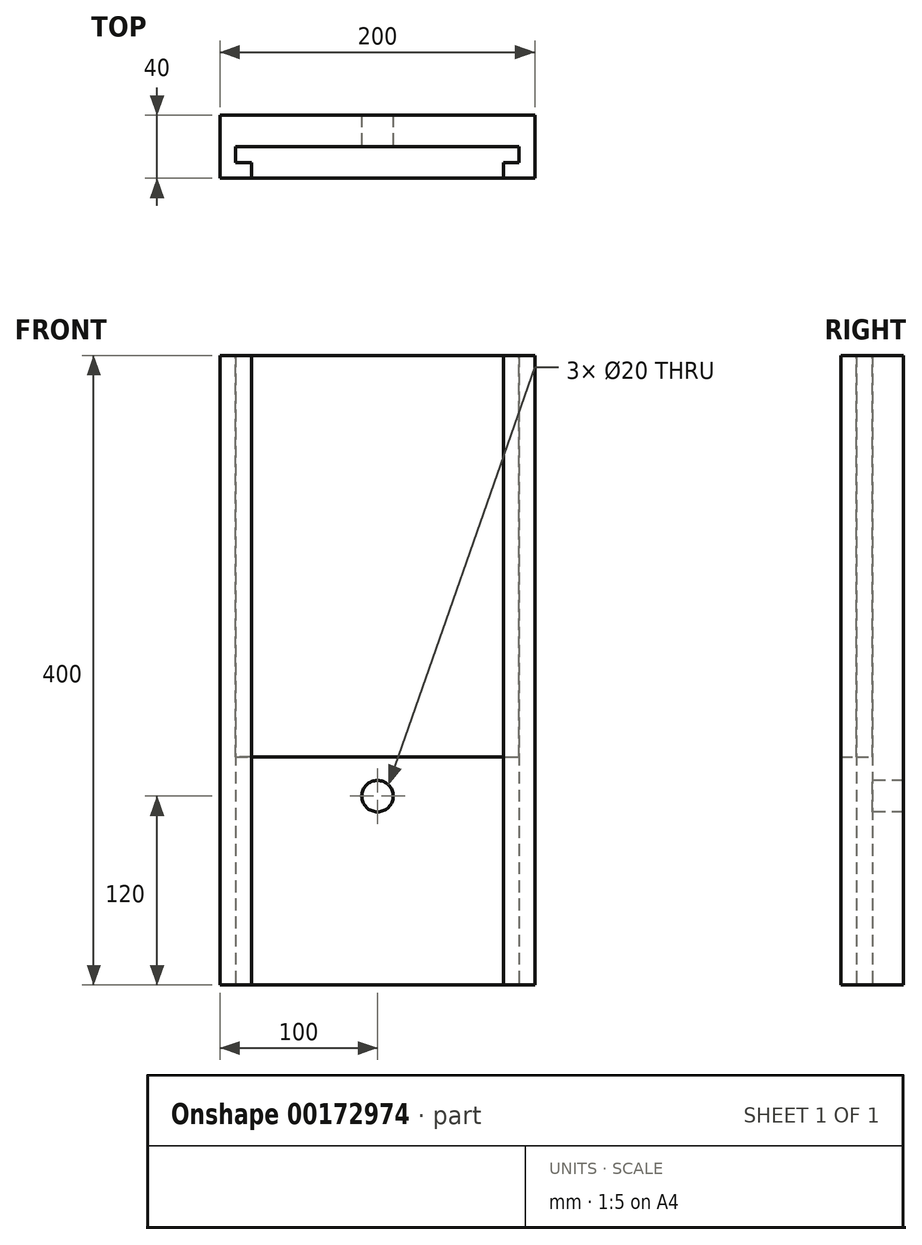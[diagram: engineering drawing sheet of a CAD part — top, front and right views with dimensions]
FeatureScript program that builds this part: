
annotation { "Feature Type Name" : "Feature", "Feature Type Description" : "" }
export const myFeature = defineFeature(function(context is Context, id is Id, definition is map)
    precondition{}
    {
        {
            var Q0;
            Q0=qCreatedBy(makeId("Top.planeOp"),FACE);
            var sketch = newSketch(context, id + "F0", { "sketchPlane" : qUnion([Q0])});
            skLineSegment(sketch, "E0", {"start": v(0, 40) * mm, "end": v(100, 40) * mm});
            skLineSegment(sketch, "E1", {"start": v(100, 40) * mm, "end": v(100, 0) * mm});
            skLineSegment(sketch, "E2", {"start": v(100, 0) * mm, "end": v(80, 0) * mm});
            skLineSegment(sketch, "E3", {"start": v(80, 0) * mm, "end": v(80, 10) * mm});
            skLineSegment(sketch, "E4", {"start": v(80, 10) * mm, "end": v(90, 10) * mm});
            skLineSegment(sketch, "E5", {"start": v(90, 10) * mm, "end": v(90, 20) * mm});
            skLineSegment(sketch, "E6", {"start": v(90, 20) * mm, "end": v(0, 20) * mm});
            skLineSegment(sketch, "E7", {"start": v(0, 40) * mm, "end": v(0, 0) * mm, "construction": true});
            skLineSegment(sketch, "E8.MirrorCS", {"start": v(0, 40) * mm, "end": v(-100, 40) * mm});
            skLineSegment(sketch, "E9.MirrorCS", {"start": v(-100, 40) * mm, "end": v(-100, 0) * mm});
            skLineSegment(sketch, "E10.MirrorCS", {"start": v(-100, 0) * mm, "end": v(-80, 0) * mm});
            skLineSegment(sketch, "E11.MirrorCS", {"start": v(-80, 0) * mm, "end": v(-80, 10) * mm});
            skLineSegment(sketch, "E12.MirrorCS", {"start": v(-80, 10) * mm, "end": v(-90, 10) * mm});
            skLineSegment(sketch, "E13.MirrorCS", {"start": v(-90, 10) * mm, "end": v(-90, 20) * mm});
            skLineSegment(sketch, "E14.MirrorCS", {"start": v(-90, 20) * mm, "end": v(0, 20) * mm});
            skSolve(sketch);
        }
        {
            var Q0;
            Q0=makeQuery(id+"F0.imprint","IMPRINT",FACE,{"disambiguationData":[TD([[makeQuery(id+"F0.imprint","IMPRINT",EDGE,{"derivedFrom":sQuery(id+"F0.wireOp",EDGE,"E0")}),-1.0]])]});
            extrude(context, id + "F1", {"entities" : qUnion([Q0]), "depth" : 280 * mm, "hasSecondDirection" : true, "secondDirectionOppositeDirection" : true, "secondDirectionDepth" : 120 * mm});
        }
        {
            var Q0;
            Q0=makeQuery(id+"F1.opExtrude","SWEPT_FACE",FACE,{"disambiguationData":[OSD([sQuery(id+"F0.wireOp",EDGE,"E6"),sQuery(id+"F0.wireOp",EDGE,"E14.MirrorCS")])]});
            var sketch = newSketch(context, id + "F2", { "sketchPlane" : qUnion([Q0])});
            skCircle(sketch, "E15", {"center": v(0, 0) * mm, "radius": 10 * mm});
            skSolve(sketch);
        }
        {
            var Q0;
            Q0 = qSketchRegion(id + "F2", true);
            extrude(context, id + "F3", {"entities" : qUnion([Q0]), "operationType" : NewBodyOperationType.REMOVE, "oppositeDirection" : true, "depth" : 20 * mm});
        }
        {
            var Q0;
            Q0=makeQuery(id+"F1.opExtrude","CAP_FACE",FACE,{"disambiguationData":[OSD([sQuery(id+"F0.wireOp",EDGE,"E0"),sQuery(id+"F0.wireOp",EDGE,"E1"),sQuery(id+"F0.wireOp",EDGE,"E2"),sQuery(id+"F0.wireOp",EDGE,"E3"),sQuery(id+"F0.wireOp",EDGE,"E4"),sQuery(id+"F0.wireOp",EDGE,"E5"),sQuery(id+"F0.wireOp",EDGE,"E6"),sQuery(id+"F0.wireOp",EDGE,"E8.MirrorCS"),sQuery(id+"F0.wireOp",EDGE,"E9.MirrorCS"),sQuery(id+"F0.wireOp",EDGE,"E10.MirrorCS"),sQuery(id+"F0.wireOp",EDGE,"E11.MirrorCS"),sQuery(id+"F0.wireOp",EDGE,"E12.MirrorCS"),sQuery(id+"F0.wireOp",EDGE,"E13.MirrorCS"),sQuery(id+"F0.wireOp",EDGE,"E14.MirrorCS")])],"isStart":false});
            var sketch = newSketch(context, id + "F4", { "sketchPlane" : qUnion([Q0])});
            skLineSegment(sketch, "E16", {"start": v(-90, 20) * mm, "end": v(-90, 10) * mm});
            skLineSegment(sketch, "E17", {"start": v(-90, 10) * mm, "end": v(-80, 10) * mm});
            skLineSegment(sketch, "E18", {"start": v(-80, 10) * mm, "end": v(-80, 0) * mm});
            skLineSegment(sketch, "E19", {"start": v(-80, 0) * mm, "end": v(80, 0) * mm});
            skLineSegment(sketch, "E20", {"start": v(80, 0) * mm, "end": v(80, 10) * mm});
            skLineSegment(sketch, "E21", {"start": v(80, 10) * mm, "end": v(90, 10) * mm});
            skLineSegment(sketch, "E22", {"start": v(90, 10) * mm, "end": v(90, 20) * mm});
            skLineSegment(sketch, "E23", {"start": v(90, 20) * mm, "end": v(-90, 20) * mm});
            skSolve(sketch);
        }
        {
            var Q0;
            Q0 = qSketchRegion(id + "F4", true);
            extrude(context, id + "F5", {"entities" : qUnion([Q0]), "oppositeDirection" : true, "depth" : 255 * mm});
        }
    });
